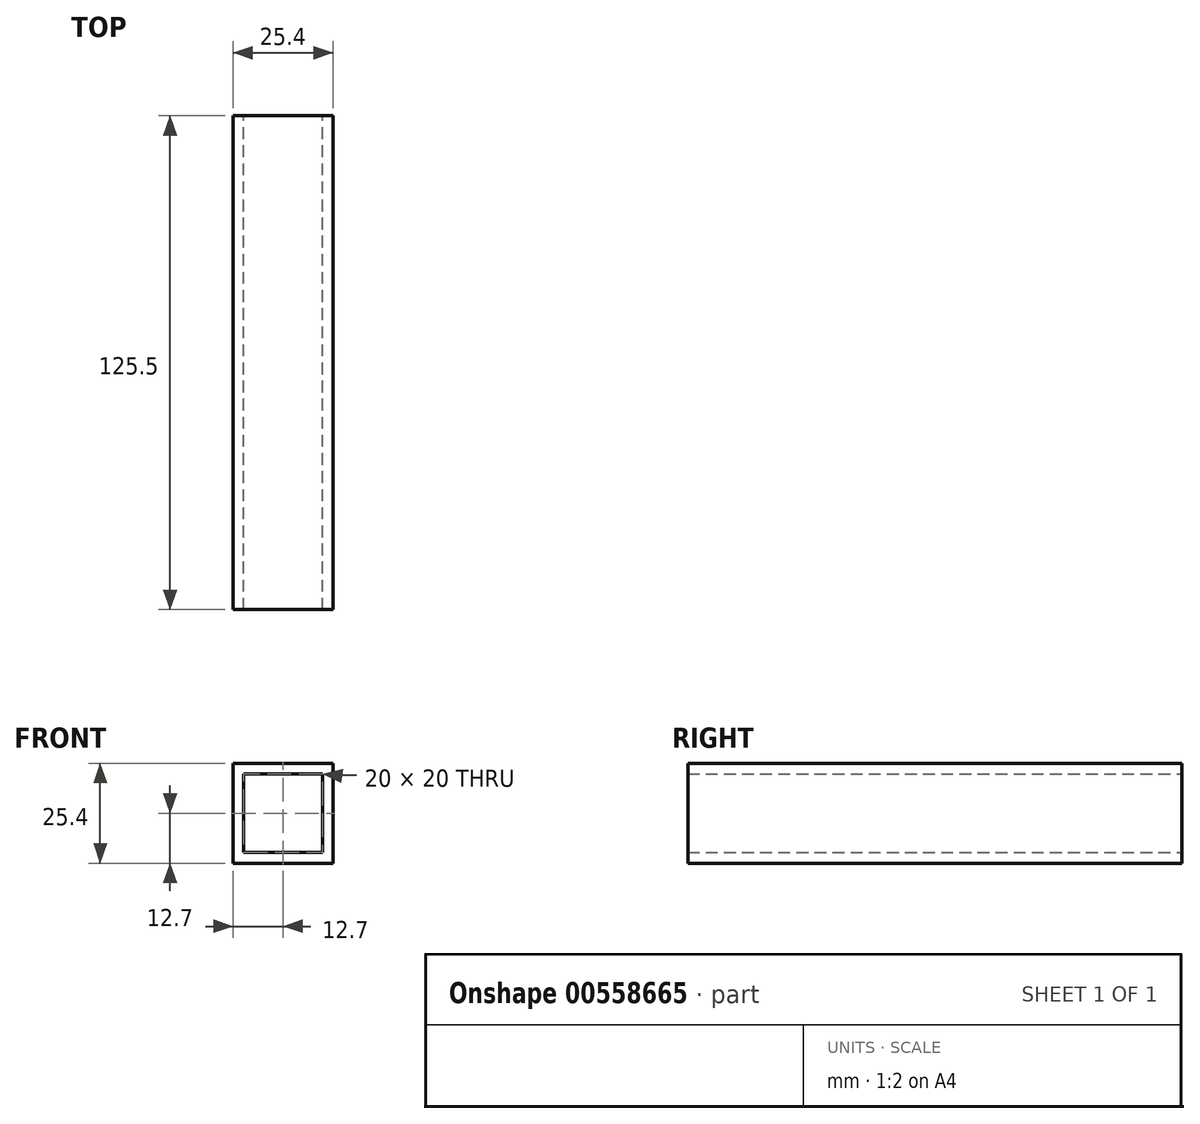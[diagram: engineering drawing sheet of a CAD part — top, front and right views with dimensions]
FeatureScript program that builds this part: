
annotation { "Feature Type Name" : "Feature", "Feature Type Description" : "" }
export const myFeature = defineFeature(function(context is Context, id is Id, definition is map)
    precondition{}
    {
        {
            var Q0;
            Q0=qCreatedBy(makeId("Front.planeOp"),FACE);
            var sketch = newSketch(context, id + "F0", { "sketchPlane" : qUnion([Q0])});
            skLineSegment(sketch, "E0.bottom", {"start": v(-12.7, -12.7) * mm, "end": v(12.7, -12.7) * mm});
            skLineSegment(sketch, "E0.top", {"start": v(-12.7, 12.7) * mm, "end": v(12.7, 12.7) * mm});
            skLineSegment(sketch, "E0.left", {"start": v(-12.7, -12.7) * mm, "end": v(-12.7, 12.7) * mm});
            skLineSegment(sketch, "E0.right", {"start": v(12.7, -12.7) * mm, "end": v(12.7, 12.7) * mm});
            skPoint(sketch, "E0.middle", {"position": v(0, 0) * mm});
            skLineSegment(sketch, "E1.bottom", {"start": v(-10, -10) * mm, "end": v(10, -10) * mm});
            skLineSegment(sketch, "E1.top", {"start": v(-10, 10) * mm, "end": v(10, 10) * mm});
            skLineSegment(sketch, "E1.left", {"start": v(-10, -10) * mm, "end": v(-10, 10) * mm});
            skLineSegment(sketch, "E1.right", {"start": v(10, -10) * mm, "end": v(10, 10) * mm});
            skSolve(sketch);
        }
        {
            var Q0;
            Q0=makeQuery(id+"F0.imprint","IMPRINT",FACE,{"disambiguationData":[TD([[makeQuery(id+"F0.imprint","IMPRINT",EDGE,{"derivedFrom":sQuery(id+"F0.wireOp",EDGE,"E0.bottom")}),1.0]])]});
            extrude(context, id + "F1", {"entities" : qUnion([Q0]), "depth" : 125.5 * mm, "offsetDistance" : 25 * mm});
        }
    });
